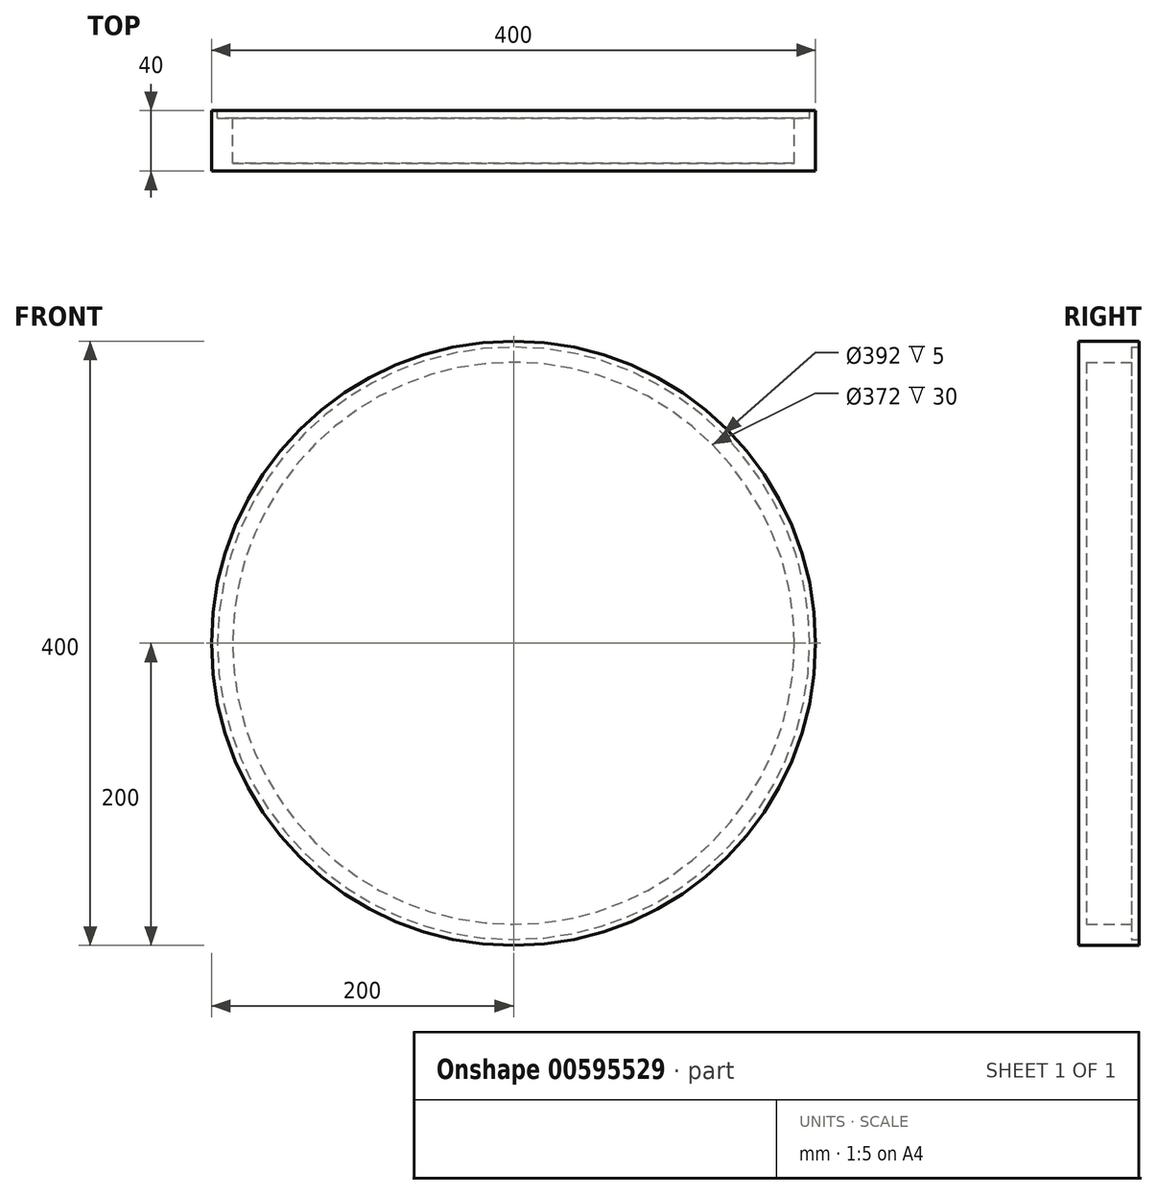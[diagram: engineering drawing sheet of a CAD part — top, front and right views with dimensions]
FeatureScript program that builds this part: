
annotation { "Feature Type Name" : "Feature", "Feature Type Description" : "" }
export const myFeature = defineFeature(function(context is Context, id is Id, definition is map)
    precondition{}
    {
        {
            var Q0;
            Q0=qCreatedBy(makeId("Front.planeOp"),FACE);
            var sketch = newSketch(context, id + "F0", { "sketchPlane" : qUnion([Q0])});
            skCircle(sketch, "E0", {"center": v(0, 0) * mm, "radius": 200 * mm});
            skSolve(sketch);
        }
        {
            var Q0;
            Q0=makeQuery(id+"F0.imprint","IMPRINT",FACE,{"disambiguationData":[TD([[makeQuery(id+"F0.imprint","IMPRINT",EDGE,{"derivedFrom":sQuery(id+"F0.wireOp",EDGE,"E0")}),1.0]])]});
            extrude(context, id + "F1", {"entities" : qUnion([Q0]), "depth" : 40 * mm, "offsetDistance" : 25 * mm});
        }
        {
            var Q0;
            Q0=makeQuery(id+"F1.opExtrude","CAP_FACE",FACE,{"disambiguationData":[OSD([sQuery(id+"F0.wireOp",EDGE,"E0")])],"isStart":true});
            var sketch = newSketch(context, id + "F2", { "sketchPlane" : qUnion([Q0])});
            skCircle(sketch, "E1", {"center": v(0, 0) * mm, "radius": 196 * mm});
            skSolve(sketch);
        }
        {
            var Q0;
            Q0=makeQuery(id+"F1.opExtrude","CAP_FACE",FACE,{"disambiguationData":[OSD([sQuery(id+"F0.wireOp",EDGE,"E0")])],"isStart":false});
            var sketch = newSketch(context, id + "F3", { "sketchPlane" : qUnion([Q0])});
            skLineSegment(sketch, "E2", {"start": v(0, 200) * mm, "end": v(0, -200) * mm});
            skLineSegment(sketch, "E3", {"start": v(200, 0) * mm, "end": v(-200, 0) * mm});
            skLineSegment(sketch, "E4", {"start": v(-141.42, -141.42) * mm, "end": v(0, 0) * mm});
            skLineSegment(sketch, "E5", {"start": v(0, 0) * mm, "end": v(141.42, 141.42) * mm});
            skLineSegment(sketch, "E6", {"start": v(0, 0) * mm, "end": v(141.42, -141.42) * mm});
            skLineSegment(sketch, "E7", {"start": v(0, 0) * mm, "end": v(-141.42, 141.42) * mm});
            skCircle(sketch, "E8", {"center": v(-113.14, 113.14) * mm, "radius": 15 * mm});
            skCircle(sketch, "E9", {"center": v(0, 0) * mm, "radius": 160 * mm});
            skCircle(sketch, "E10", {"center": v(0, 160) * mm, "radius": 15 * mm});
            skCircle(sketch, "E11", {"center": v(113.14, 113.14) * mm, "radius": 15 * mm});
            skCircle(sketch, "E12", {"center": v(160, 0) * mm, "radius": 15 * mm});
            skCircle(sketch, "E13", {"center": v(113.14, -113.14) * mm, "radius": 15 * mm});
            skCircle(sketch, "E14", {"center": v(0, -160) * mm, "radius": 15 * mm});
            skCircle(sketch, "E15", {"center": v(-113.14, -113.14) * mm, "radius": 15 * mm});
            skCircle(sketch, "E16", {"center": v(-160, 0) * mm, "radius": 15 * mm});
            skSolve(sketch);
        }
        {
            var Q0;
            Q0=makeQuery(id+"F2.imprint","IMPRINT",FACE,{"disambiguationData":[TD([[makeQuery(id+"F2.imprint","IMPRINT",EDGE,{"derivedFrom":sQuery(id+"F2.wireOp",EDGE,"E1")}),1.0]])]});
            extrude(context, id + "F4", {"entities" : qUnion([Q0]), "operationType" : NewBodyOperationType.REMOVE, "oppositeDirection" : true, "depth" : 5 * mm, "offsetDistance" : 25 * mm});
        }
        {
            var Q0;
            Q0=makeQuery(id+"F4.boolean.opBoolean","COPY",FACE,{"derivedFrom":makeQuery(id+"F4.opExtrude","CAP_FACE",FACE,{"disambiguationData":[OSD([sQuery(id+"F2.wireOp",EDGE,"E1")])],"isStart":false})});
            var sketch = newSketch(context, id + "F5", { "sketchPlane" : qUnion([Q0])});
            skCircle(sketch, "E17", {"center": v(0, 0) * mm, "radius": 186 * mm});
            skSolve(sketch);
        }
        {
            var Q0;
            Q0=makeQuery(id+"F5.imprint","IMPRINT",FACE,{"disambiguationData":[TD([[makeQuery(id+"F5.imprint","IMPRINT",EDGE,{"derivedFrom":sQuery(id+"F5.wireOp",EDGE,"E17")}),1.0]])]});
            extrude(context, id + "F6", {"entities" : qUnion([Q0]), "operationType" : NewBodyOperationType.REMOVE, "oppositeDirection" : true, "depth" : 30 * mm, "offsetDistance" : 25 * mm});
        }
    });
